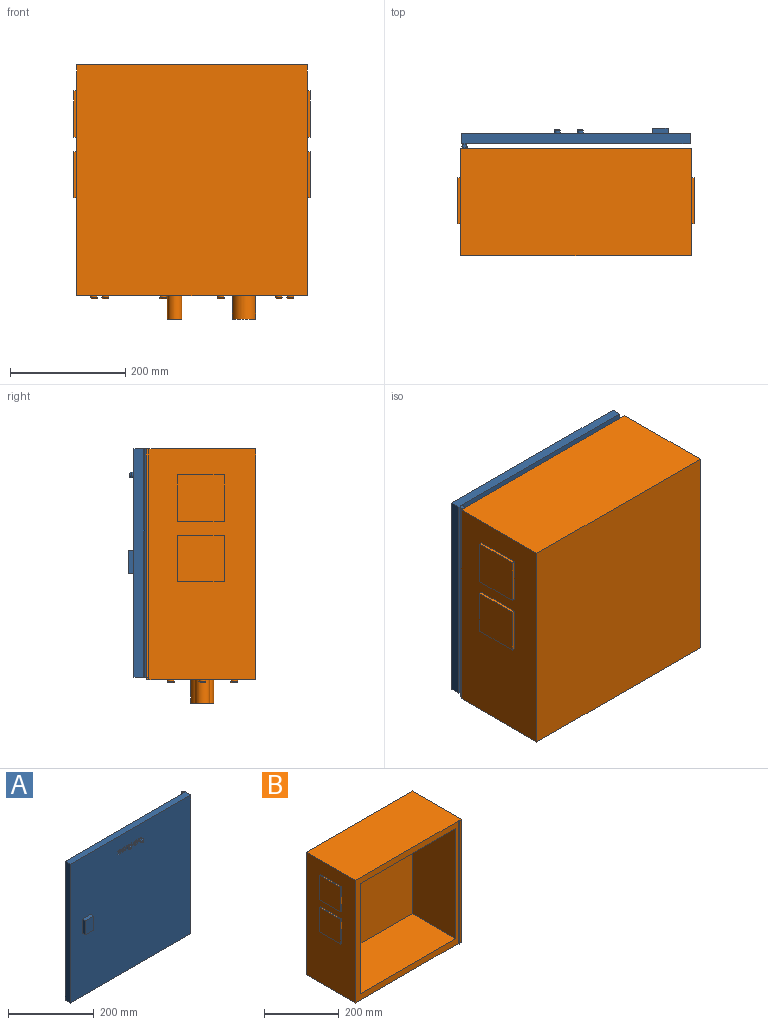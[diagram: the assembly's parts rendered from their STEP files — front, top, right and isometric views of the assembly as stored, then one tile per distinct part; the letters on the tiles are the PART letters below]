
ASSEMBLY  parts=2 mates=1
PART A: 119 faces, bbox 395x35.5x395 mm
  f0: plane 395x395mm, normal (0,-1,0), area 154455.3mm2, adj f1,f2,f3,f4,f6,f8,f10,f11
  f1: plane 395x17mm, normal (1,0,0), area 6715mm2, adj f0,f2,f4,f18
  f2: plane 395x25.5mm, normal (0,0,1), area 6766.3mm2, adj f0,f1,f3,f5,f15,f16,f17,f18
  f3: plane 395x17mm, normal (-1,0,0), area 6715mm2, adj f0,f2,f4,f5
  f4: plane 395x25.5mm, normal (0,0,-1), area 6766.3mm2, adj f0,f1,f3,f5,f15,f16,f17,f18
  f5: plane 395x389.5mm, normal (0,1,0), area 153852.5mm2, adj f2,f3,f4,f15
  f6: cylinder r=5mm len=10mm, axis (0,1,0), area 157.1mm2, adj f0,f118
  f7: plane 5x5mm, normal (0,-1,0), area 19.6mm2, adj f118
  f8: cylinder r=5mm len=10mm, axis (0,1,0), area 157.1mm2, adj f0,f117
  f9: plane 5x5mm, normal (0,-1,0), area 19.6mm2, adj f117
  f10: plane 27x10mm, normal (0,0,-1), area 270mm2, adj f0,f11,f13,f14
  f11: plane 40x10mm, normal (1,0,0), area 400mm2, adj f0,f10,f12,f14
  f12: plane 27x10mm, normal (0,0,1), area 270mm2, adj f0,f11,f13,f14
  f13: plane 40x10mm, normal (-1,0,0), area 400mm2, adj f0,f10,f12,f14
  f14: plane 40x27mm, normal (0,-1,0), area 1080mm2, adj f10,f11,f12,f13
  f15: plane 395x0.63mm, normal (-1,0,0), area 247.7mm2, adj f2,f4,f5,f16
  f16: cylinder r=4mm len=395mm, axis (0,0,1), area 9129mm2, adj f2,f4,f15,f17
  f17: plane 395x0.63mm, normal (1,0,0), area 247.7mm2, adj f2,f4,f16,f18
  f18: plane 395x3.5mm, normal (0,1,0), area 1382.5mm2, adj f1,f2,f4,f17
  f19: plane 2.06x0.5mm, normal (1,0,0), area 1mm2, adj f20,f36,f37,f115
  f20: plane 2.93x0.5mm, normal (0,0,-1), area 1.5mm2, adj f19,f21,f37,f115
  f21: plane 3.37x2.23mm, normal (-0.83,0,0.55), area 2mm2, adj f20,f22,f37,f115
  f22: extruded ~1.33x0.74mm, area 0.8mm2, adj f21,f23,f37,f115
  f23: plane 0.5x0.07mm, normal (0,0,1), area 0mm2, adj f22,f24,f37,f115
  f24: extruded ~1.14x0.5mm, area 0.6mm2, adj f23,f36,f37,f115
  f25: plane 1.46x0.5mm, normal (0,0,1), area 0.7mm2, adj f0,f26,f35,f37
  f26: plane 2x0.5mm, normal (-1,0,0), area 1mm2, adj f0,f25,f27,f37
  f27: plane 1.46x0.5mm, normal (0,0,-1), area 0.7mm2, adj f0,f26,f28,f37
  f28: plane 7.65x0.5mm, normal (-1,0,0), area 3.8mm2, adj f0,f27,f29,f37
  f29: plane 2.37x0.5mm, normal (0,0,-1), area 1.2mm2, adj f0,f28,f30,f37
  f30: plane 7.85x5.33mm, normal (0.83,0,-0.56), area 4.7mm2, adj f0,f29,f31,f37
  f31: plane 1.79x0.5mm, normal (1,0,0), area 0.9mm2, adj f0,f30,f32,f37
  f32: plane 5.19x0.5mm, normal (0,0,1), area 2.6mm2, adj f0,f31,f33,f37
  f33: plane 2.52x0.5mm, normal (1,0,0), area 1.3mm2, adj f0,f32,f34,f37
  f34: plane 2.51x0.5mm, normal (0,0,1), area 1.3mm2, adj f0,f33,f35,f37
  f35: plane 2.52x0.5mm, normal (-1,0,0), area 1.3mm2, adj f0,f25,f34,f37
  f36: extruded ~1.5x0.5mm, area 0.7mm2, adj f19,f24,f37,f115
  f37: plane 12.16x9.17mm, normal (0,-1,0), area 56mm2, adj f19,f20,f21,f22,f23,f24,f25,f26
  f38: plane 2.6x0.5mm, normal (0,0,-1), area 1.3mm2, adj f0,f39,f47,f48
  f39: plane 7.24x2.3mm, normal (0.95,0,-0.3), area 3.8mm2, adj f0,f38,f40,f48
  f40: extruded ~2.68x0.63mm, area 1.4mm2, adj f0,f39,f41,f48
  f41: extruded ~1.18x0.5mm, area 0.6mm2, adj f0,f40,f42,f48
  f42: extruded ~1.49x0.5mm, area 0.8mm2, adj f0,f41,f43,f48
  f43: plane 7.24x2.29mm, normal (-0.95,0,-0.3), area 3.8mm2, adj f0,f42,f44,f48
  f44: plane 2.6x0.5mm, normal (0,0,-1), area 1.3mm2, adj f0,f43,f45,f48
  f45: plane 12.16x4.13mm, normal (0.95,0,0.32), area 6.4mm2, adj f0,f44,f46,f48
  f46: plane 2.81x0.5mm, normal (0,0,1), area 1.4mm2, adj f0,f45,f47,f48
  f47: plane 12.16x4.13mm, normal (-0.95,0,0.32), area 6.4mm2, adj f0,f38,f46,f48
  f48: plane 12.16x11.07mm, normal (0,-1,0), area 57mm2, adj f38,f39,f40,f41,f42,f43,f44,f45
  f49: plane 2.57x0.5mm, normal (0,0,1), area 1.3mm2, adj f0,f50,f58,f59
  f50: plane 12.16x0.5mm, normal (-1,0,0), area 6.1mm2, adj f0,f49,f51,f59
  f51: plane 2.11x0.5mm, normal (0,0,-1), area 1.1mm2, adj f0,f50,f52,f59
  f52: plane 3.92x3.12mm, normal (0.62,0,-0.78), area 2.5mm2, adj f0,f51,f53,f59
  f53: plane 1.55x1.24mm, normal (0.78,0,0.63), area 1mm2, adj f0,f52,f54,f59
  f54: plane 1.4x1.12mm, normal (-0.63,0,0.78), area 0.9mm2, adj f0,f53,f55,f59
  f55: extruded ~0.89x0.84mm, area 0.6mm2, adj f0,f54,f56,f59
  f56: plane 1.26x0.5mm, normal (1,0,-0.03), area 0.6mm2, adj f0,f55,f57,f59
  f57: plane 1.16x0.5mm, normal (1,0,-0.02), area 0.6mm2, adj f0,f56,f58,f59
  f58: plane 7.04x0.5mm, normal (1,0,0), area 3.5mm2, adj f0,f49,f57,f59
  f59: plane 12.16x6.03mm, normal (0,-1,0), area 38.3mm2, adj f49,f50,f51,f52,f53,f54,f55,f56
  f60: plane 2.6x0.5mm, normal (0,0,-1), area 1.3mm2, adj f0,f61,f69,f70
  f61: plane 7.24x2.3mm, normal (0.95,0,-0.3), area 3.8mm2, adj f0,f60,f62,f70
  f62: extruded ~2.68x0.63mm, area 1.4mm2, adj f0,f61,f63,f70
  f63: extruded ~1.18x0.5mm, area 0.6mm2, adj f0,f62,f64,f70
  f64: extruded ~1.49x0.5mm, area 0.8mm2, adj f0,f63,f65,f70
  f65: plane 7.24x2.29mm, normal (-0.95,0,-0.3), area 3.8mm2, adj f0,f64,f66,f70
  f66: plane 2.6x0.5mm, normal (0,0,-1), area 1.3mm2, adj f0,f65,f67,f70
  f67: plane 12.16x4.13mm, normal (0.95,0,0.32), area 6.4mm2, adj f0,f66,f68,f70
  f68: plane 2.81x0.5mm, normal (0,0,1), area 1.4mm2, adj f0,f67,f69,f70
  f69: plane 12.16x4.13mm, normal (-0.95,0,0.32), area 6.4mm2, adj f0,f60,f68,f70
  f70: plane 12.16x11.07mm, normal (0,-1,0), area 57mm2, adj f60,f61,f62,f63,f64,f65,f66,f67
  f71: plane 2.06x0.5mm, normal (1,0,0), area 1mm2, adj f72,f88,f89,f116
  f72: plane 2.93x0.5mm, normal (0,0,-1), area 1.5mm2, adj f71,f73,f89,f116
  f73: plane 3.37x2.23mm, normal (-0.83,0,0.55), area 2mm2, adj f72,f74,f89,f116
  f74: extruded ~1.33x0.74mm, area 0.8mm2, adj f73,f75,f89,f116
  f75: plane 0.5x0.07mm, normal (0,0,1), area 0mm2, adj f74,f76,f89,f116
  f76: extruded ~1.14x0.5mm, area 0.6mm2, adj f75,f88,f89,f116
  f77: plane 1.46x0.5mm, normal (0,0,1), area 0.7mm2, adj f0,f78,f87,f89
  f78: plane 2x0.5mm, normal (-1,0,0), area 1mm2, adj f0,f77,f79,f89
  f79: plane 1.46x0.5mm, normal (0,0,-1), area 0.7mm2, adj f0,f78,f80,f89
  f80: plane 7.65x0.5mm, normal (-1,0,0), area 3.8mm2, adj f0,f79,f81,f89
  f81: plane 2.37x0.5mm, normal (0,0,-1), area 1.2mm2, adj f0,f80,f82,f89
  f82: plane 7.85x5.33mm, normal (0.83,0,-0.56), area 4.7mm2, adj f0,f81,f83,f89
  f83: plane 1.79x0.5mm, normal (1,0,0), area 0.9mm2, adj f0,f82,f84,f89
  f84: plane 5.19x0.5mm, normal (0,0,1), area 2.6mm2, adj f0,f83,f85,f89
  f85: plane 2.52x0.5mm, normal (1,0,0), area 1.3mm2, adj f0,f84,f86,f89
  f86: plane 2.51x0.5mm, normal (0,0,1), area 1.3mm2, adj f0,f85,f87,f89
  f87: plane 2.52x0.5mm, normal (-1,0,0), area 1.3mm2, adj f0,f77,f86,f89
  f88: extruded ~1.5x0.5mm, area 0.7mm2, adj f71,f76,f89,f116
  f89: plane 12.16x9.17mm, normal (0,-1,0), area 56mm2, adj f71,f72,f73,f74,f75,f76,f77,f78
  f90: plane 8.5x0.5mm, normal (0,0,1), area 4.3mm2, adj f0,f91,f113,f114
  f91: plane 2.16x0.5mm, normal (-1,0,0), area 1.1mm2, adj f0,f90,f92,f114
  f92: plane 5.3x0.5mm, normal (0,0,-1), area 2.7mm2, adj f0,f91,f93,f114
  f93: plane 0.5x0.11mm, normal (-1,0,0), area 0.1mm2, adj f0,f92,f94,f114
  f94: plane 1.57x1.47mm, normal (-0.69,0,0.73), area 1.1mm2, adj f0,f93,f95,f114
  f95: extruded ~2.21x2.18mm, area 1.6mm2, adj f0,f94,f96,f114
  f96: extruded ~1.51x0.92mm, area 0.9mm2, adj f0,f95,f97,f114
  f97: extruded ~1.58x0.5mm, area 0.8mm2, adj f0,f96,f98,f114
  f98: extruded ~1.71x0.5mm, area 0.9mm2, adj f0,f97,f99,f114
  f99: extruded ~1.36x1.16mm, area 0.9mm2, adj f0,f98,f100,f114
  f100: extruded ~2.01x0.5mm, area 1mm2, adj f0,f99,f101,f114
  f101: extruded ~1.56x0.5mm, area 0.8mm2, adj f0,f100,f102,f114
  f102: extruded ~1.29x0.5mm, area 0.7mm2, adj f0,f101,f103,f114
  f103: extruded ~1.49x1.08mm, area 0.9mm2, adj f0,f102,f104,f114
  f104: plane 1.66x1.4mm, normal (0.76,0,0.65), area 1.1mm2, adj f0,f103,f105,f114
  f105: extruded ~1.39x0.92mm, area 0.8mm2, adj f0,f104,f106,f114
  f106: extruded ~1.37x0.5mm, area 0.7mm2, adj f0,f105,f107,f114
  f107: extruded ~1.08x0.5mm, area 0.6mm2, adj f0,f106,f108,f114
  f108: extruded ~1.09x0.5mm, area 0.6mm2, adj f0,f107,f109,f114
  f109: extruded ~0.95x0.5mm, area 0.5mm2, adj f0,f108,f110,f114
  f110: extruded ~0.99x0.6mm, area 0.6mm2, adj f0,f109,f111,f114
  f111: extruded ~1.93x1.77mm, area 1.3mm2, adj f0,f110,f112,f114
  f112: plane 3.09x3.05mm, normal (0.71,0,-0.7), area 2.2mm2, adj f0,f111,f113,f114
  f113: plane 1.79x0.5mm, normal (1,0,0), area 0.9mm2, adj f0,f90,f112,f114
  f114: plane 12.34x8.53mm, normal (0,-1,0), area 55.1mm2, adj f90,f91,f92,f93,f94,f95,f96,f97
  f115: plane 4.7x3.04mm, normal (0,-1,0), area 6.6mm2, adj f19,f20,f21,f22,f23,f24,f36
  f116: plane 4.7x3.04mm, normal (0,-1,0), area 6.6mm2, adj f71,f72,f73,f74,f75,f76,f88
  f117: torus R=2.5mm, axis (0,-1,0), area 101mm2, adj f8,f9
  f118: torus R=2.5mm, axis (0,-1,0), area 101mm2, adj f6,f7
PART B: 73 faces, bbox 410x189.5x440 mm
  f0: plane 400x185mm, normal (1,0,0), area 61200mm2, adj f1,f2,f5,f13,f53,f54,f55,f56
  f1: plane 400x189.5mm, normal (0,0,-1), area 71128.3mm2, adj f0,f3,f4,f5,f11,f12,f13,f14
  f2: plane 400x189.5mm, normal (0,0,1), area 74006.8mm2, adj f0,f3,f4,f5,f11,f12,f13,f14
  f3: plane 400x392mm, normal (0,-1,0), area 27200mm2, adj f1,f2,f4,f6,f7,f8,f9,f18
  f4: plane 400x185mm, normal (-1,0,0), area 61200mm2, adj f1,f2,f3,f5,f63,f64,f65,f66
  f5: plane 400x400mm, normal (0,1,0), area 160000mm2, adj f0,f1,f2,f4
  f6: plane 360x165mm, normal (-1,0,0), area 59400mm2, adj f3,f7,f9,f10
  f7: plane 360x165mm, normal (0,0,-1), area 59400mm2, adj f3,f6,f8,f10
  f8: plane 360x165mm, normal (1,0,0), area 59400mm2, adj f3,f7,f9,f10
  f9: plane 360x165mm, normal (0,0,1), area 59400mm2, adj f3,f6,f8,f10
  f10: plane 360x360mm, normal (0,-1,0), area 129600mm2, adj f6,f7,f8,f9
  f11: cylinder r=4mm len=400mm, axis (0,0,1), area 5026.5mm2, adj f1,f2,f12,f16
  f12: plane 400x0.5mm, normal (0,-1,0), area 200mm2, adj f1,f2,f11,f17
  f13: plane 400x6mm, normal (0,-1,0), area 2400mm2, adj f0,f1,f2,f14
  f14: plane 400x0.11mm, normal (1,0,0), area 45mm2, adj f1,f2,f13,f15
  f15: cylinder r=4.5mm len=400mm, axis (0,0,1), area 2424.1mm2, adj f1,f2,f14,f16
  f16: plane 400x0.5mm, normal (0,-1,0), area 200mm2, adj f1,f2,f11,f15
  f17: cylinder r=4.5mm len=400mm, axis (0,0,1), area 2424.1mm2, adj f1,f2,f12,f18
  f18: plane 400x0.11mm, normal (-1,0,0), area 45mm2, adj f1,f2,f3,f17
  f19: cylinder r=6mm len=12mm, axis (0,0,1), area 113.1mm2, adj f1,f48
  f20: plane 8x8mm, normal (0,0,-1), area 50.3mm2, adj f48
  f21: cylinder r=6mm len=12mm, axis (0,0,1), area 113.1mm2, adj f1,f47
  f22: plane 8x8mm, normal (0,0,-1), area 50.3mm2, adj f47
  f23: cylinder r=6mm len=12mm, axis (0,0,1), area 113.1mm2, adj f1,f46
  f24: plane 8x8mm, normal (0,0,-1), area 50.3mm2, adj f46
  f25: cylinder r=6mm len=12mm, axis (0,0,1), area 113.1mm2, adj f1,f45
  f26: plane 8x8mm, normal (0,0,-1), area 50.3mm2, adj f45
  f27: cylinder r=6mm len=12mm, axis (0,0,1), area 113.1mm2, adj f1,f44
  f28: plane 8x8mm, normal (0,0,-1), area 50.3mm2, adj f44
  f29: cylinder r=6mm len=12mm, axis (0,0,1), area 113.1mm2, adj f1,f43
  f30: plane 8x8mm, normal (0,0,-1), area 50.3mm2, adj f43
  f31: cylinder r=6mm len=12mm, axis (0,0,1), area 113.1mm2, adj f1,f42
  f32: plane 8x8mm, normal (0,0,-1), area 50.3mm2, adj f42
  f33: cylinder r=6mm len=12mm, axis (0,0,1), area 113.1mm2, adj f1,f41
  f34: plane 8x8mm, normal (0,0,-1), area 50.3mm2, adj f41
  f35: cylinder r=6mm len=12mm, axis (0,0,1), area 113.1mm2, adj f1,f40
  f36: plane 8x8mm, normal (0,0,-1), area 50.3mm2, adj f40
  f37: cylinder r=6mm len=12mm, axis (0,0,1), area 113.1mm2, adj f1,f39
  f38: plane 8x8mm, normal (0,0,-1), area 50.3mm2, adj f39
  f39: torus R=4mm, axis (0,0,-1), area 104.1mm2, adj f37,f38
  f40: torus R=4mm, axis (0,0,-1), area 104.1mm2, adj f35,f36
  f41: torus R=4mm, axis (0,0,-1), area 104.1mm2, adj f33,f34
  f42: torus R=4mm, axis (0,0,-1), area 104.1mm2, adj f31,f32
  f43: torus R=4mm, axis (0,0,-1), area 104.1mm2, adj f29,f30
  f44: torus R=4mm, axis (0,0,-1), area 104.1mm2, adj f27,f28
  f45: torus R=4mm, axis (0,0,-1), area 104.1mm2, adj f25,f26
  f46: torus R=4mm, axis (0,0,-1), area 104.1mm2, adj f23,f24
  f47: torus R=4mm, axis (0,0,-1), area 104.1mm2, adj f21,f22
  f48: torus R=4mm, axis (0,0,-1), area 104.1mm2, adj f19,f20
  f49: cylinder r=20mm len=40mm, axis (0,0,1), area 5026.5mm2, adj f1,f50
  f50: plane 40x40mm, normal (0,0,-1), area 1256.6mm2, adj f49
  f51: cylinder r=12.5mm len=40mm, axis (0,0,1), area 3141.6mm2, adj f1,f52
  f52: plane 25x25mm, normal (0,0,-1), area 490.9mm2, adj f51
  f53: plane 80x5mm, normal (0,0,-1), area 400mm2, adj f0,f54,f56,f57
  f54: plane 80x5mm, normal (0,1,0), area 400mm2, adj f0,f53,f55,f57
  f55: plane 80x5mm, normal (0,0,1), area 400mm2, adj f0,f54,f56,f57
  f56: plane 80x5mm, normal (0,-1,0), area 400mm2, adj f0,f53,f55,f57
  f57: plane 80x80mm, normal (1,0,0), area 6400mm2, adj f53,f54,f55,f56
  f58: plane 80x5mm, normal (0,0,-1), area 400mm2, adj f0,f59,f61,f62
  f59: plane 80x5mm, normal (0,1,0), area 400mm2, adj f0,f58,f60,f62
  f60: plane 80x5mm, normal (0,0,1), area 400mm2, adj f0,f59,f61,f62
  f61: plane 80x5mm, normal (0,-1,0), area 400mm2, adj f0,f58,f60,f62
  f62: plane 80x80mm, normal (1,0,0), area 6400mm2, adj f58,f59,f60,f61
  f63: plane 80x5mm, normal (0,0,-1), area 400mm2, adj f4,f64,f66,f67
  f64: plane 80x5mm, normal (0,-1,0), area 400mm2, adj f4,f63,f65,f67
  f65: plane 80x5mm, normal (0,0,1), area 400mm2, adj f4,f64,f66,f67
  f66: plane 80x5mm, normal (0,1,0), area 400mm2, adj f4,f63,f65,f67
  f67: plane 80x80mm, normal (-1,0,0), area 6400mm2, adj f63,f64,f65,f66
  f68: plane 80x5mm, normal (0,0,-1), area 400mm2, adj f4,f69,f71,f72
  f69: plane 80x5mm, normal (0,-1,0), area 400mm2, adj f4,f68,f70,f72
  f70: plane 80x5mm, normal (0,0,1), area 400mm2, adj f4,f69,f71,f72
  f71: plane 80x5mm, normal (0,1,0), area 400mm2, adj f4,f68,f70,f72
  f72: plane 80x80mm, normal (-1,0,0), area 6400mm2, adj f68,f69,f70,f71
PLACE A rot(axis=(0,0,-1),180deg) t=(1.4,101.49,202.5)mm
PLACE B rot(axis=(0,0,1),180deg) t=(1.4,-92.51,200)mm
MATE revolute B.f11 <-> A.f16  axis (0,0,1) through (-191.6,96.99,400)mm
